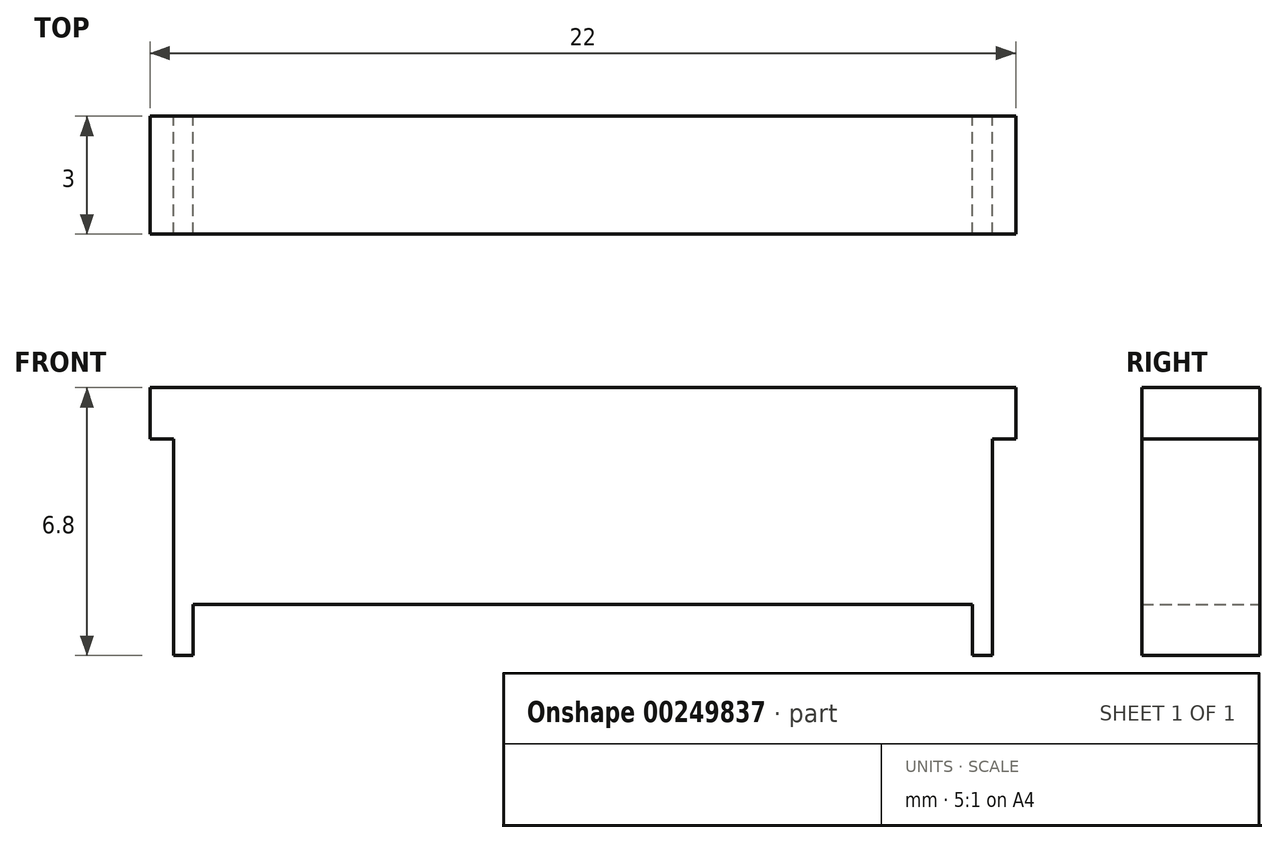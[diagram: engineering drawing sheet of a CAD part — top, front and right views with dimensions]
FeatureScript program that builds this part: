
annotation { "Feature Type Name" : "Feature", "Feature Type Description" : "" }
export const myFeature = defineFeature(function(context is Context, id is Id, definition is map)
    precondition{}
    {
        {
            var Q0;
            Q0=qCreatedBy(makeId("Front.planeOp"),FACE);
            var sketch = newSketch(context, id + "F0", { "sketchPlane" : qUnion([Q0])});
            skLineSegment(sketch, "E0.bottom", {"start": v(0.5, 0) * mm, "end": v(20.3, 0) * mm});
            skLineSegment(sketch, "E0.left", {"start": v(0, 0) * mm, "end": v(0, 4.2) * mm});
            skLineSegment(sketch, "E0.right", {"start": v(20.8, 0) * mm, "end": v(20.8, 4.2) * mm});
            skLineSegment(sketch, "E1.bottom", {"start": v(-0.6, 4.2) * mm, "end": v(0, 4.2) * mm});
            skLineSegment(sketch, "E1.top", {"start": v(-0.6, 5.5) * mm, "end": v(21.4, 5.5) * mm});
            skLineSegment(sketch, "E1.left", {"start": v(-0.6, 4.2) * mm, "end": v(-0.6, 5.5) * mm});
            skLineSegment(sketch, "E1.right", {"start": v(21.4, 4.2) * mm, "end": v(21.4, 5.5) * mm});
            skLineSegment(sketch, "E2.trimOffspring", {"start": v(20.8, 4.2) * mm, "end": v(21.4, 4.2) * mm});
            skLineSegment(sketch, "E3", {"start": v(0, 0) * mm, "end": v(0, -1.3) * mm});
            skLineSegment(sketch, "E4", {"start": v(0, -1.3) * mm, "end": v(0.5, -1.3) * mm});
            skLineSegment(sketch, "E5", {"start": v(0.5, -1.3) * mm, "end": v(0.5, 0) * mm});
            skLineSegment(sketch, "E6", {"start": v(20.8, 0) * mm, "end": v(20.8, -1.3) * mm});
            skLineSegment(sketch, "E7", {"start": v(20.8, -1.3) * mm, "end": v(20.3, -1.3) * mm});
            skLineSegment(sketch, "E8", {"start": v(20.3, -1.3) * mm, "end": v(20.3, 0) * mm});
            skSolve(sketch);
        }
        {
            var Q0;
            Q0 = qSketchRegion(id + "F0", true);
            extrude(context, id + "F1", {"entities" : qUnion([Q0]), "depth" : 3 * mm});
        }
    });
